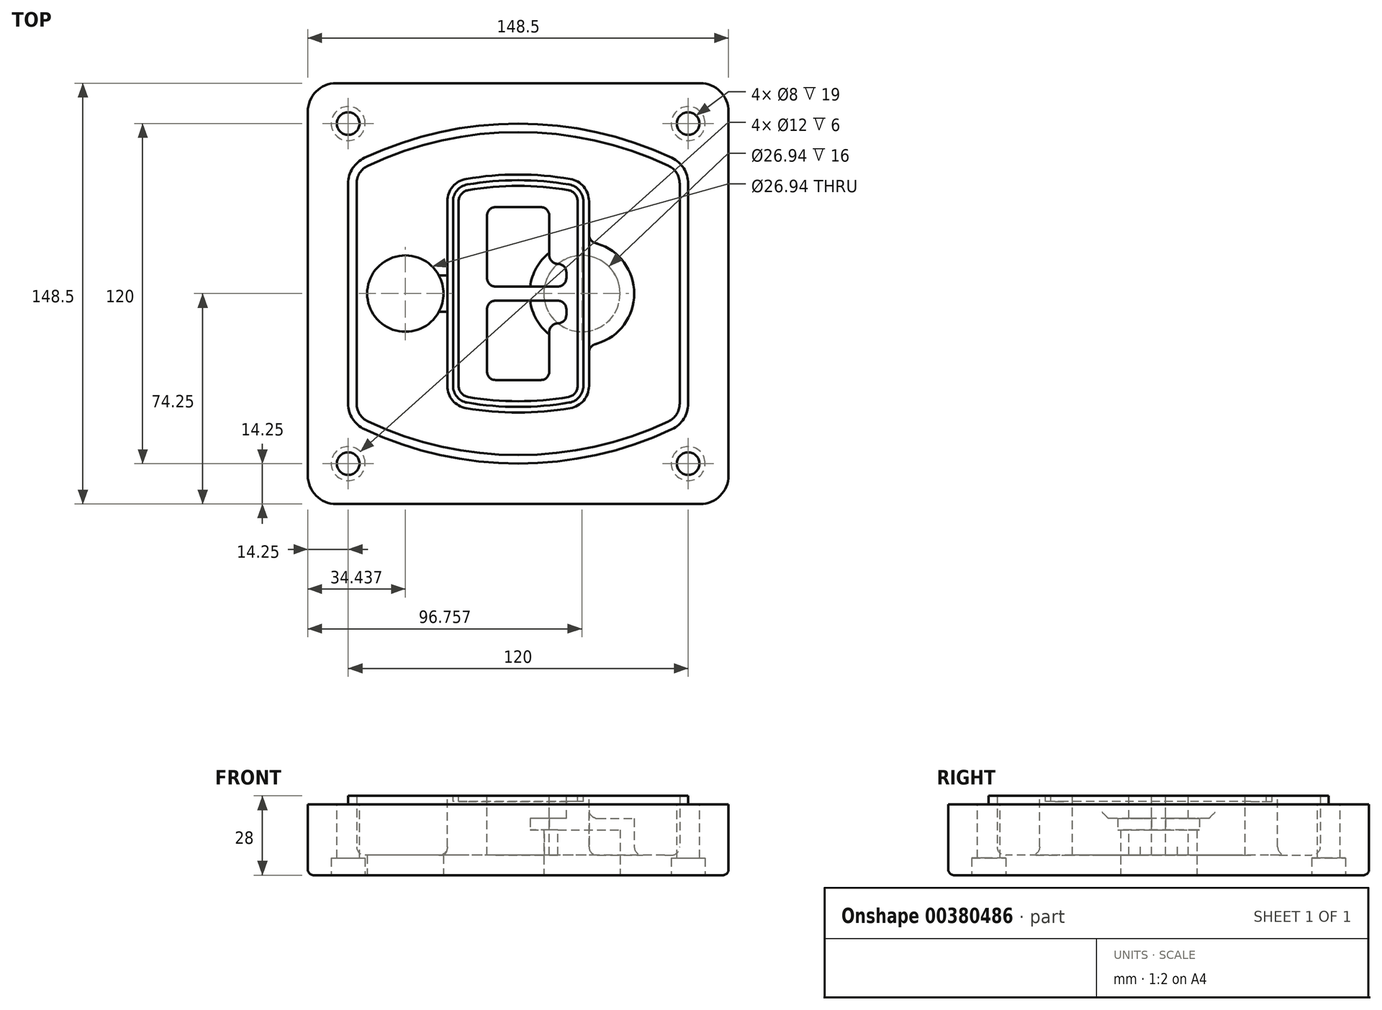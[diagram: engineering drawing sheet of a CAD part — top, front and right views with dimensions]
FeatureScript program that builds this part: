
annotation { "Feature Type Name" : "Feature", "Feature Type Description" : "" }
export const myFeature = defineFeature(function(context is Context, id is Id, definition is map)
    precondition{}
    {
        {
            var Q0;
            Q0=qCreatedBy(makeId("Top.planeOp"),FACE);
            var sketch = newSketch(context, id + "F0", { "sketchPlane" : qUnion([Q0])});
            skPoint(sketch, "E0.rect.middle", {"position": v(0, 0) * mm});
            skLineSegment(sketch, "E1.bottom", {"start": v(-64.25, -74.25) * mm, "end": v(64.25, -74.25) * mm});
            skLineSegment(sketch, "E1.top", {"start": v(-64.25, 74.25) * mm, "end": v(64.25, 74.25) * mm});
            skLineSegment(sketch, "E1.left", {"start": v(-74.25, -64.25) * mm, "end": v(-74.25, 64.25) * mm});
            skLineSegment(sketch, "E1.right", {"start": v(74.25, -64.25) * mm, "end": v(74.25, 64.25) * mm});
            skLineSegment(sketch, "E2", {"start": v(-74.25, 74.25) * mm, "end": v(74.25, -74.25) * mm, "construction": true});
            skLineSegment(sketch, "E3", {"start": v(74.25, 74.25) * mm, "end": v(-74.25, -74.25) * mm, "construction": true});
            skCircle(sketch, "E4", {"center": v(-60, 60) * mm, "radius": 4 * mm});
            skCircle(sketch, "E5", {"center": v(60, 60) * mm, "radius": 4 * mm});
            skCircle(sketch, "E6", {"center": v(60, -60) * mm, "radius": 4 * mm});
            skCircle(sketch, "E7", {"center": v(-60, -60) * mm, "radius": 4 * mm});
            skLineSegment(sketch, "E8", {"start": v(-60, 60) * mm, "end": v(60, 60) * mm, "construction": true});
            skLineSegment(sketch, "E9", {"start": v(60, 60) * mm, "end": v(60, -60) * mm, "construction": true});
            skLineSegment(sketch, "E10", {"start": v(60, -60) * mm, "end": v(-60, -60) * mm, "construction": true});
            skLineSegment(sketch, "E11", {"start": v(-60, -60) * mm, "end": v(-60, 60) * mm, "construction": true});
            skLineSegment(sketch, "E12", {"start": v(-60, 38.83) * mm, "end": v(-60, -38.83) * mm});
            skLineSegment(sketch, "E13", {"start": v(60, 38.83) * mm, "end": v(60, -38.83) * mm});
            skArc(sketch, "E14", {"start": v(54.26, 47.88) * mm, "mid": v(0, 60) * mm, "end": v(-54.26, 47.88) * mm});
            skArc(sketch, "E15", {"start": v(-54.26, -47.88) * mm, "mid": v(0, -60) * mm, "end": v(54.26, -47.88) * mm});
            skLineSegment(sketch, "E16", {"start": v(-60, 0) * mm, "end": v(60, 0) * mm, "construction": true});
            skPoint(sketch, "E17.visualSharp", {"position": v(-60, -45) * mm});
            skArc(sketch, "E17.filletArc", {"start": v(-60, -38.83) * mm, "mid": v(-58.44, -44.2) * mm, "end": v(-54.26, -47.88) * mm});
            skPoint(sketch, "E18.visualSharp", {"position": v(-60, 45) * mm});
            skArc(sketch, "E18.filletArc", {"start": v(-54.26, 47.88) * mm, "mid": v(-58.44, 44.2) * mm, "end": v(-60, 38.83) * mm});
            skPoint(sketch, "E19.visualSharp", {"position": v(60, 45) * mm});
            skArc(sketch, "E19.filletArc", {"start": v(60, 38.83) * mm, "mid": v(58.44, 44.2) * mm, "end": v(54.26, 47.88) * mm});
            skPoint(sketch, "E20.visualSharp", {"position": v(60, -45) * mm});
            skArc(sketch, "E20.filletArc", {"start": v(54.26, -47.88) * mm, "mid": v(58.44, -44.2) * mm, "end": v(60, -38.83) * mm});
            skPoint(sketch, "E21.visualSharp", {"position": v(-74.25, 74.25) * mm});
            skArc(sketch, "E21.filletArc", {"start": v(-64.25, 74.25) * mm, "mid": v(-71.32, 71.32) * mm, "end": v(-74.25, 64.25) * mm});
            skPoint(sketch, "E22.visualSharp", {"position": v(74.25, 74.25) * mm});
            skArc(sketch, "E22.filletArc", {"start": v(74.25, 64.25) * mm, "mid": v(71.32, 71.32) * mm, "end": v(64.25, 74.25) * mm});
            skPoint(sketch, "E23.visualSharp", {"position": v(74.25, -74.25) * mm});
            skArc(sketch, "E23.filletArc", {"start": v(64.25, -74.25) * mm, "mid": v(71.32, -71.32) * mm, "end": v(74.25, -64.25) * mm});
            skPoint(sketch, "E24.visualSharp", {"position": v(-74.25, -74.25) * mm});
            skArc(sketch, "E24.filletArc", {"start": v(-74.25, -64.25) * mm, "mid": v(-71.32, -71.32) * mm, "end": v(-64.25, -74.25) * mm});
            skArc(sketch, "E25.0", {"start": v(57, 38.83) * mm, "mid": v(55.9, 42.58) * mm, "end": v(52.98, 45.17) * mm});
            skLineSegment(sketch, "E25.1", {"start": v(57, 38.83) * mm, "end": v(57, -38.83) * mm});
            skArc(sketch, "E25.2", {"start": v(52.98, -45.17) * mm, "mid": v(55.9, -42.58) * mm, "end": v(57, -38.83) * mm});
            skArc(sketch, "E25.3", {"start": v(-52.98, -45.17) * mm, "mid": v(0, -57) * mm, "end": v(52.98, -45.17) * mm});
            skArc(sketch, "E25.4", {"start": v(-57, -38.83) * mm, "mid": v(-55.9, -42.58) * mm, "end": v(-52.98, -45.17) * mm});
            skArc(sketch, "E25.5", {"start": v(52.98, 45.17) * mm, "mid": v(0, 57) * mm, "end": v(-52.98, 45.17) * mm});
            skLineSegment(sketch, "E25.6", {"start": v(-57, 38.83) * mm, "end": v(-57, -38.83) * mm});
            skArc(sketch, "E25.7", {"start": v(-52.98, 45.17) * mm, "mid": v(-55.9, 42.58) * mm, "end": v(-57, 38.83) * mm});
            skArc(sketch, "E26.0", {"start": v(-55.96, 51.5) * mm, "mid": v(-61.82, 46.33) * mm, "end": v(-64, 38.83) * mm});
            skArc(sketch, "E26.1", {"start": v(55.96, 51.5) * mm, "mid": v(0, 64) * mm, "end": v(-55.96, 51.5) * mm});
            skArc(sketch, "E26.2", {"start": v(64, 38.83) * mm, "mid": v(61.82, 46.33) * mm, "end": v(55.96, 51.5) * mm});
            skLineSegment(sketch, "E26.3", {"start": v(64, 38.83) * mm, "end": v(64, -38.83) * mm});
            skArc(sketch, "E26.4", {"start": v(55.96, -51.5) * mm, "mid": v(61.82, -46.33) * mm, "end": v(64, -38.83) * mm});
            skLineSegment(sketch, "E26.5", {"start": v(-64, 38.83) * mm, "end": v(-64, -38.83) * mm});
            skArc(sketch, "E26.6", {"start": v(-55.96, -51.5) * mm, "mid": v(0, -64) * mm, "end": v(55.96, -51.5) * mm});
            skArc(sketch, "E26.7", {"start": v(-64, -38.83) * mm, "mid": v(-61.82, -46.33) * mm, "end": v(-55.96, -51.5) * mm});
            skLineSegment(sketch, "E27", {"start": v(0, 74.25) * mm, "end": v(0, 104.25) * mm});
            skPoint(sketch, "E27.endSnap0", {"position": v(0, 74.25) * mm});
            skCircle(sketch, "E28", {"center": v(0, 104.25) * mm, "radius": 6 * mm});
            skLineSegment(sketch, "E29", {"start": v(-7.18, 74.25) * mm, "end": v(-7.18, 92.25) * mm});
            skLineSegment(sketch, "E30", {"start": v(-12.94, 92.25) * mm, "end": v(-28.79, 74.25) * mm});
            skLineSegment(sketch, "E31", {"start": v(-12.94, 104.25) * mm, "end": v(-12.94, 92.25) * mm});
            skLineSegment(sketch, "E32", {"start": v(15.13, 92.25) * mm, "end": v(27.03, 74.25) * mm});
            skLineSegment(sketch, "E33", {"start": v(15.13, 92.25) * mm, "end": v(15.13, 104.25) * mm});
            skArc(sketch, "E34", {"start": v(15.13, 104.25) * mm, "mid": v(1.1, 124.55) * mm, "end": v(-12.94, 104.25) * mm});
            skSolve(sketch);
        }
        {
            var Q0;
            Q0=makeQuery(id+"F0.imprint","IMPRINT",FACE,{"disambiguationData":[TD([[makeQuery(id+"F0.imprint","IMPRINT",EDGE,{"derivedFrom":sQuery(id+"F0.wireOp",EDGE,"E1.bottom")}),1.0]])]});
            var Q1;
            Q1=makeQuery(id+"F0.imprint","IMPRINT",FACE,{"disambiguationData":[TD([[makeQuery(id+"F0.imprint","IMPRINT",EDGE,{"derivedFrom":sQuery(id+"F0.wireOp",EDGE,"E12")}),1.0]])]});
            var Q2;
            Q2=makeQuery(id+"F0.imprint","IMPRINT",FACE,{"disambiguationData":[TD([[makeQuery(id+"F0.imprint","IMPRINT",EDGE,{"derivedFrom":sQuery(id+"F0.wireOp",EDGE,"E25.0")}),1.0]])]});
            var Q3;
            Q3=makeQuery(id+"F0.imprint","IMPRINT",FACE,{"disambiguationData":[TD([[makeQuery(id+"F0.imprint","IMPRINT",EDGE,{"derivedFrom":sQuery(id+"F0.wireOp",EDGE,"E12")}),-1.0]])]});
            extrude(context, id + "F1", {"entities" : qUnion([Q0, Q1, Q2, Q3]), "oppositeDirection" : true, "depth" : 25 * mm});
        }
        {
            var Q0;
            Q0=makeQuery(id+"F0.imprint","IMPRINT",FACE,{"disambiguationData":[TD([[makeQuery(id+"F0.imprint","IMPRINT",EDGE,{"derivedFrom":sQuery(id+"F0.wireOp",EDGE,"E12")}),1.0]])]});
            extrude(context, id + "F2", {"entities" : qUnion([Q0]), "operationType" : NewBodyOperationType.ADD, "depth" : 3 * mm});
        }
        {
            var Q0;
            Q0=makeQuery(id+"F0.imprint","IMPRINT",FACE,{"disambiguationData":[TD([[makeQuery(id+"F0.imprint","IMPRINT",EDGE,{"derivedFrom":sQuery(id+"F0.wireOp",EDGE,"E25.0")}),1.0]])]});
            extrude(context, id + "F3", {"entities" : qUnion([Q0]), "operationType" : NewBodyOperationType.REMOVE, "oppositeDirection" : true, "depth" : 18 * mm});
        }
        {
            var Q0;
            Q0=makeQuery(id+"F2.opExtrude","CAP_FACE",FACE,{"disambiguationData":[OSD([sQuery(id+"F0.wireOp",EDGE,"E12"),sQuery(id+"F0.wireOp",EDGE,"E13"),sQuery(id+"F0.wireOp",EDGE,"E14"),sQuery(id+"F0.wireOp",EDGE,"E15"),sQuery(id+"F0.wireOp",EDGE,"E17.filletArc"),sQuery(id+"F0.wireOp",EDGE,"E18.filletArc"),sQuery(id+"F0.wireOp",EDGE,"E19.filletArc"),sQuery(id+"F0.wireOp",EDGE,"E20.filletArc"),sQuery(id+"F0.wireOp",EDGE,"E25.0"),sQuery(id+"F0.wireOp",EDGE,"E25.1"),sQuery(id+"F0.wireOp",EDGE,"E25.2"),sQuery(id+"F0.wireOp",EDGE,"E25.3"),sQuery(id+"F0.wireOp",EDGE,"E25.4"),sQuery(id+"F0.wireOp",EDGE,"E25.5"),sQuery(id+"F0.wireOp",EDGE,"E25.6"),sQuery(id+"F0.wireOp",EDGE,"E25.7")])],"isStart":false});
            var sketch = newSketch(context, id + "F4", { "sketchPlane" : qUnion([Q0])});
            skArc(sketch, "E35.0", {"start": v(-18.34, -40.45) * mm, "mid": v(0, -42) * mm, "end": v(18.34, -40.45) * mm});
            skArc(sketch, "E36.0", {"start": v(18.34, 40.45) * mm, "mid": v(0, 42) * mm, "end": v(-18.34, 40.45) * mm});
            skLineSegment(sketch, "E37", {"start": v(-25, 32.57) * mm, "end": v(-25, -32.57) * mm});
            skLineSegment(sketch, "E38", {"start": v(25, 32.57) * mm, "end": v(25, -32.57) * mm});
            skLineSegment(sketch, "E39", {"start": v(-25, 39.1) * mm, "end": v(25, 39.1) * mm, "construction": true});
            skLineSegment(sketch, "E40", {"start": v(-25, -39.1) * mm, "end": v(25, -39.1) * mm, "construction": true});
            skPoint(sketch, "E41.visualSharp", {"position": v(-25, 39.1) * mm});
            skArc(sketch, "E41.filletArc", {"start": v(-18.34, 40.45) * mm, "mid": v(-23.11, 37.73) * mm, "end": v(-25, 32.57) * mm});
            skPoint(sketch, "E42.visualSharp", {"position": v(25, 39.1) * mm});
            skArc(sketch, "E42.filletArc", {"start": v(25, 32.57) * mm, "mid": v(23.11, 37.73) * mm, "end": v(18.34, 40.45) * mm});
            skPoint(sketch, "E43.visualSharp", {"position": v(25, -39.1) * mm});
            skArc(sketch, "E43.filletArc", {"start": v(18.34, -40.45) * mm, "mid": v(23.11, -37.73) * mm, "end": v(25, -32.57) * mm});
            skPoint(sketch, "E44.visualSharp", {"position": v(-25, -39.1) * mm});
            skArc(sketch, "E44.filletArc", {"start": v(-25, -32.57) * mm, "mid": v(-23.11, -37.73) * mm, "end": v(-18.34, -40.45) * mm});
            skArc(sketch, "E45.0", {"start": v(52.98, 45.17) * mm, "mid": v(0, 57) * mm, "end": v(-52.98, 45.17) * mm});
            skArc(sketch, "E45.1", {"start": v(-52.98, 45.17) * mm, "mid": v(-55.9, 42.58) * mm, "end": v(-57, 38.83) * mm});
            skLineSegment(sketch, "E45.2", {"start": v(-57, 38.83) * mm, "end": v(-57, -38.83) * mm});
            skArc(sketch, "E45.3", {"start": v(-57, -38.83) * mm, "mid": v(-55.9, -42.58) * mm, "end": v(-52.98, -45.17) * mm});
            skArc(sketch, "E45.4", {"start": v(-52.98, -45.17) * mm, "mid": v(0, -57) * mm, "end": v(52.98, -45.17) * mm});
            skArc(sketch, "E45.5", {"start": v(52.98, -45.17) * mm, "mid": v(55.9, -42.58) * mm, "end": v(57, -38.83) * mm});
            skLineSegment(sketch, "E45.6", {"start": v(57, 38.83) * mm, "end": v(57, -38.83) * mm});
            skArc(sketch, "E45.7", {"start": v(57, 38.83) * mm, "mid": v(55.9, 42.58) * mm, "end": v(52.98, 45.17) * mm});
            skLineSegment(sketch, "E46.0", {"start": v(23, 32.57) * mm, "end": v(23, -32.57) * mm});
            skArc(sketch, "E46.1", {"start": v(18, -38.48) * mm, "mid": v(21.58, -36.44) * mm, "end": v(23, -32.57) * mm});
            skArc(sketch, "E46.2", {"start": v(-18, -38.48) * mm, "mid": v(0, -40) * mm, "end": v(18, -38.48) * mm});
            skArc(sketch, "E46.3", {"start": v(-23, -32.57) * mm, "mid": v(-21.58, -36.44) * mm, "end": v(-18, -38.48) * mm});
            skLineSegment(sketch, "E46.4", {"start": v(-23, 32.57) * mm, "end": v(-23, -32.57) * mm});
            skArc(sketch, "E46.5", {"start": v(23, 32.57) * mm, "mid": v(21.58, 36.44) * mm, "end": v(18, 38.48) * mm});
            skArc(sketch, "E46.6", {"start": v(-18, 38.48) * mm, "mid": v(-21.58, 36.44) * mm, "end": v(-23, 32.57) * mm});
            skArc(sketch, "E46.7", {"start": v(18, 38.48) * mm, "mid": v(0, 40) * mm, "end": v(-18, 38.48) * mm});
            skArc(sketch, "E47.0", {"start": v(21, 32.57) * mm, "mid": v(20.06, 35.15) * mm, "end": v(17.67, 36.5) * mm});
            skLineSegment(sketch, "E47.1", {"start": v(21, 32.57) * mm, "end": v(21, -32.57) * mm});
            skArc(sketch, "E47.2", {"start": v(17.67, -36.5) * mm, "mid": v(20.06, -35.15) * mm, "end": v(21, -32.57) * mm});
            skArc(sketch, "E47.3", {"start": v(-17.67, -36.5) * mm, "mid": v(0, -38) * mm, "end": v(17.67, -36.5) * mm});
            skArc(sketch, "E47.4", {"start": v(-21, -32.57) * mm, "mid": v(-20.06, -35.15) * mm, "end": v(-17.67, -36.5) * mm});
            skArc(sketch, "E47.5", {"start": v(17.67, 36.5) * mm, "mid": v(0, 38) * mm, "end": v(-17.67, 36.5) * mm});
            skLineSegment(sketch, "E47.6", {"start": v(-21, 32.57) * mm, "end": v(-21, -32.57) * mm});
            skArc(sketch, "E47.7", {"start": v(-17.67, 36.5) * mm, "mid": v(-20.06, 35.15) * mm, "end": v(-21, 32.57) * mm});
            skLineSegment(sketch, "E48", {"start": v(-25, 0) * mm, "end": v(25, 0) * mm, "construction": true});
            skLineSegment(sketch, "E49", {"start": v(-11, 5.5) * mm, "end": v(-11, 27.5) * mm});
            skLineSegment(sketch, "E50", {"start": v(-8, 30.5) * mm, "end": v(8, 30.5) * mm});
            skLineSegment(sketch, "E51", {"start": v(11, 27.5) * mm, "end": v(11, 13.5) * mm});
            skLineSegment(sketch, "E52", {"start": v(14, 10.5) * mm, "end": v(14, 10.5) * mm});
            skLineSegment(sketch, "E53", {"start": v(17, 7.5) * mm, "end": v(17, 5.5) * mm});
            skLineSegment(sketch, "E54", {"start": v(14, 2.5) * mm, "end": v(-8, 2.5) * mm});
            skPoint(sketch, "E55.visualSharp", {"position": v(-11, 30.5) * mm});
            skArc(sketch, "E55.filletArc", {"start": v(-8, 30.5) * mm, "mid": v(-10.12, 29.62) * mm, "end": v(-11, 27.5) * mm});
            skPoint(sketch, "E56.visualSharp", {"position": v(11, 30.5) * mm});
            skArc(sketch, "E56.filletArc", {"start": v(11, 27.5) * mm, "mid": v(10.12, 29.62) * mm, "end": v(8, 30.5) * mm});
            skPoint(sketch, "E57.visualSharp", {"position": v(11, 10.5) * mm});
            skArc(sketch, "E57.filletArc", {"start": v(11, 13.5) * mm, "mid": v(11.88, 11.38) * mm, "end": v(14, 10.5) * mm});
            skPoint(sketch, "E58.visualSharp", {"position": v(17, 10.5) * mm});
            skArc(sketch, "E58.filletArc", {"start": v(17, 7.5) * mm, "mid": v(16.12, 9.62) * mm, "end": v(14, 10.5) * mm});
            skPoint(sketch, "E59.visualSharp", {"position": v(17, 2.5) * mm});
            skArc(sketch, "E59.filletArc", {"start": v(14, 2.5) * mm, "mid": v(16.12, 3.38) * mm, "end": v(17, 5.5) * mm});
            skPoint(sketch, "E60.visualSharp", {"position": v(-11, 2.5) * mm});
            skArc(sketch, "E60.filletArc", {"start": v(-11, 5.5) * mm, "mid": v(-10.12, 3.38) * mm, "end": v(-8, 2.5) * mm});
            skLineSegment(sketch, "E61.0.MirrorCS", {"start": v(14, -2.5) * mm, "end": v(-8, -2.5) * mm});
            skArc(sketch, "E62.0.MirrorCS", {"start": v(-11, -5.5) * mm, "mid": v(-10.12, -3.38) * mm, "end": v(-8, -2.5) * mm});
            skLineSegment(sketch, "E63.0.MirrorCS", {"start": v(-11, -5.5) * mm, "end": v(-11, -27.5) * mm});
            skArc(sketch, "E64.0.MirrorCS", {"start": v(-8, -30.5) * mm, "mid": v(-10.12, -29.62) * mm, "end": v(-11, -27.5) * mm});
            skLineSegment(sketch, "E65.0.MirrorCS", {"start": v(-8, -30.5) * mm, "end": v(8, -30.5) * mm});
            skArc(sketch, "E66.0.MirrorCS", {"start": v(11, -27.5) * mm, "mid": v(10.12, -29.62) * mm, "end": v(8, -30.5) * mm});
            skLineSegment(sketch, "E67.0.MirrorCS", {"start": v(11, -27.5) * mm, "end": v(11, -13.5) * mm});
            skArc(sketch, "E68.0.MirrorCS", {"start": v(11, -13.5) * mm, "mid": v(11.88, -11.38) * mm, "end": v(14, -10.5) * mm});
            skArc(sketch, "E69.0.MirrorCS", {"start": v(17, -7.5) * mm, "mid": v(16.12, -9.62) * mm, "end": v(14, -10.5) * mm});
            skLineSegment(sketch, "E70.0.MirrorCS", {"start": v(17, -7.5) * mm, "end": v(17, -5.5) * mm});
            skArc(sketch, "E71.0.MirrorCS", {"start": v(14, -2.5) * mm, "mid": v(16.12, -3.38) * mm, "end": v(17, -5.5) * mm});
            skSolve(sketch);
        }
        {
            var Q0;
            Q0=makeQuery(id+"F4.imprint","IMPRINT",FACE,{"disambiguationData":[TD([[makeQuery(id+"F4.imprint","IMPRINT",EDGE,{"derivedFrom":sQuery(id+"F4.wireOp",EDGE,"E35.0")}),1.0]])]});
            var Q1;
            Q1=makeQuery(id+"F4.imprint","IMPRINT",FACE,{"disambiguationData":[TD([[makeQuery(id+"F4.imprint","IMPRINT",EDGE,{"derivedFrom":sQuery(id+"F4.wireOp",EDGE,"E46.0")}),-1.0]])]});
            var Q2;
            Q2=makeQuery(id+"F4.imprint","IMPRINT",FACE,{"disambiguationData":[TD([[makeQuery(id+"F4.imprint","IMPRINT",EDGE,{"derivedFrom":sQuery(id+"F4.wireOp",EDGE,"E47.0")}),1.0]])]});
            extrude(context, id + "F5", {"entities" : qUnion([Q0, Q1, Q2]), "operationType" : NewBodyOperationType.ADD, "endBound" : BoundingType.UP_TO_NEXT, "oppositeDirection" : true, "depth" : 25 * mm});
        }
        {
            var Q0;
            Q0=makeQuery(id+"F4.imprint","IMPRINT",FACE,{"disambiguationData":[TD([[makeQuery(id+"F4.imprint","IMPRINT",EDGE,{"derivedFrom":sQuery(id+"F4.wireOp",EDGE,"E46.0")}),-1.0]])]});
            extrude(context, id + "F6", {"entities" : qUnion([Q0]), "operationType" : NewBodyOperationType.REMOVE, "oppositeDirection" : true, "depth" : 2 * mm});
        }
        {
            var Q0;
            Q0=makeQuery(id+"F1.opExtrude","CAP_FACE",FACE,{"disambiguationData":[OSD([sQuery(id+"F0.wireOp",EDGE,"E1.bottom"),sQuery(id+"F0.wireOp",EDGE,"E1.top"),sQuery(id+"F0.wireOp",EDGE,"E1.left"),sQuery(id+"F0.wireOp",EDGE,"E1.right"),sQuery(id+"F0.wireOp",EDGE,"E4"),sQuery(id+"F0.wireOp",EDGE,"E5"),sQuery(id+"F0.wireOp",EDGE,"E6"),sQuery(id+"F0.wireOp",EDGE,"E7"),sQuery(id+"F0.wireOp",EDGE,"E21.filletArc"),sQuery(id+"F0.wireOp",EDGE,"E22.filletArc"),sQuery(id+"F0.wireOp",EDGE,"E23.filletArc"),sQuery(id+"F0.wireOp",EDGE,"E24.filletArc")])],"isStart":false});
            var sketch = newSketch(context, id + "F7", { "sketchPlane" : qUnion([Q0])});
            skCircle(sketch, "E72", {"center": v(22.5, 0) * mm, "radius": 13.47 * mm});
            skCircle(sketch, "E73", {"center": v(-39.81, 0) * mm, "radius": 13.47 * mm});
            skLineSegment(sketch, "E74", {"start": v(74.25, 0) * mm, "end": v(-74.25, 0) * mm});
            skCircle(sketch, "E75", {"center": v(22.5, 0) * mm, "radius": 18.47 * mm});
            skCircle(sketch, "E76", {"center": v(60, -60) * mm, "radius": 6 * mm});
            skCircle(sketch, "E77", {"center": v(-60, -60) * mm, "radius": 6 * mm});
            skCircle(sketch, "E78", {"center": v(-60, 60) * mm, "radius": 6 * mm});
            skCircle(sketch, "E79", {"center": v(60, 60) * mm, "radius": 6 * mm});
            skSolve(sketch);
        }
        {
            var Q0;
            {var subQ1=sQuery(id+"F7.wireOp",EDGE,"E74");var subQ4=sQuery(id+"F7.wireOp",EDGE,"E72");var subQ6=makeQuery(id+"F7.imprint","INTERSECT",VERTEX,{"disambiguationData":[OD(0.0)],"derivedFrom":[subQ4,subQ1]});Q0=makeQuery(id+"F7.imprint","IMPRINT",FACE,{"disambiguationData":[TD([[makeQuery(id+"F7.imprint","IMPRINT",EDGE,{"disambiguationData":[TD([[subQ6,-1.0]])],"derivedFrom":subQ4}),-1.0]])]});}
            var Q1;
            {var subQ0=sQuery(id+"F7.wireOp",EDGE,"E74");var subQ1=sQuery(id+"F7.wireOp",EDGE,"E72");var subQ3=makeQuery(id+"F7.imprint","INTERSECT",VERTEX,{"disambiguationData":[OD(0.0)],"derivedFrom":[subQ1,subQ0]});Q1=makeQuery(id+"F7.imprint","IMPRINT",FACE,{"disambiguationData":[TD([[makeQuery(id+"F7.imprint","IMPRINT",EDGE,{"disambiguationData":[TD([[subQ3,-1.0]])],"derivedFrom":subQ1}),1.0]])]});}
            var Q2;
            {var subQ0=sQuery(id+"F7.wireOp",EDGE,"E74");var subQ1=sQuery(id+"F7.wireOp",EDGE,"E72");var subQ3=makeQuery(id+"F7.imprint","INTERSECT",VERTEX,{"disambiguationData":[OD(0.0)],"derivedFrom":[subQ1,subQ0]});Q2=makeQuery(id+"F7.imprint","IMPRINT",FACE,{"disambiguationData":[TD([[makeQuery(id+"F7.imprint","IMPRINT",EDGE,{"disambiguationData":[TD([[subQ3,1.0]])],"derivedFrom":subQ1}),1.0]])]});}
            var Q3;
            {var subQ1=sQuery(id+"F7.wireOp",EDGE,"E74");var subQ4=sQuery(id+"F7.wireOp",EDGE,"E72");var subQ6=makeQuery(id+"F7.imprint","INTERSECT",VERTEX,{"disambiguationData":[OD(0.0)],"derivedFrom":[subQ4,subQ1]});Q3=makeQuery(id+"F7.imprint","IMPRINT",FACE,{"disambiguationData":[TD([[makeQuery(id+"F7.imprint","IMPRINT",EDGE,{"disambiguationData":[TD([[subQ6,1.0]])],"derivedFrom":subQ4}),-1.0]])]});}
            extrude(context, id + "F8", {"entities" : qUnion([Q0, Q1, Q2, Q3]), "operationType" : NewBodyOperationType.ADD, "oppositeDirection" : true, "depth" : 20 * mm});
        }
        {
            var Q0;
            {var subQ0=sQuery(id+"F7.wireOp",EDGE,"E74");var subQ1=sQuery(id+"F7.wireOp",EDGE,"E72");var subQ3=makeQuery(id+"F7.imprint","INTERSECT",VERTEX,{"disambiguationData":[OD(0.0)],"derivedFrom":[subQ1,subQ0]});Q0=makeQuery(id+"F7.imprint","IMPRINT",FACE,{"disambiguationData":[TD([[makeQuery(id+"F7.imprint","IMPRINT",EDGE,{"disambiguationData":[TD([[subQ3,-1.0]])],"derivedFrom":subQ1}),1.0]])]});}
            var Q1;
            {var subQ0=sQuery(id+"F7.wireOp",EDGE,"E74");var subQ1=sQuery(id+"F7.wireOp",EDGE,"E72");var subQ3=makeQuery(id+"F7.imprint","INTERSECT",VERTEX,{"disambiguationData":[OD(0.0)],"derivedFrom":[subQ1,subQ0]});Q1=makeQuery(id+"F7.imprint","IMPRINT",FACE,{"disambiguationData":[TD([[makeQuery(id+"F7.imprint","IMPRINT",EDGE,{"disambiguationData":[TD([[subQ3,1.0]])],"derivedFrom":subQ1}),1.0]])]});}
            extrude(context, id + "F9", {"entities" : qUnion([Q0, Q1]), "operationType" : NewBodyOperationType.REMOVE, "oppositeDirection" : true, "depth" : 16 * mm});
        }
        {
            var Q0;
            {var subQ0=sQuery(id+"F7.wireOp",EDGE,"E74");var subQ1=sQuery(id+"F7.wireOp",EDGE,"E73");var subQ3=makeQuery(id+"F7.imprint","INTERSECT",VERTEX,{"disambiguationData":[OD(0.0)],"derivedFrom":[subQ1,subQ0]});Q0=makeQuery(id+"F7.imprint","IMPRINT",FACE,{"disambiguationData":[TD([[makeQuery(id+"F7.imprint","IMPRINT",EDGE,{"disambiguationData":[TD([[subQ3,-1.0]])],"derivedFrom":subQ1}),1.0]])]});}
            var Q1;
            {var subQ0=sQuery(id+"F7.wireOp",EDGE,"E74");var subQ1=sQuery(id+"F7.wireOp",EDGE,"E73");var subQ3=makeQuery(id+"F7.imprint","INTERSECT",VERTEX,{"disambiguationData":[OD(0.0)],"derivedFrom":[subQ1,subQ0]});Q1=makeQuery(id+"F7.imprint","IMPRINT",FACE,{"disambiguationData":[TD([[makeQuery(id+"F7.imprint","IMPRINT",EDGE,{"disambiguationData":[TD([[subQ3,1.0]])],"derivedFrom":subQ1}),1.0]])]});}
            extrude(context, id + "F10", {"entities" : qUnion([Q0, Q1]), "operationType" : NewBodyOperationType.REMOVE, "oppositeDirection" : true, "depth" : 25 * mm});
        }
        {
            var Q0;
            Q0=makeQuery(id+"F7.imprint","IMPRINT",FACE,{"disambiguationData":[TD([[makeQuery(id+"F7.imprint","IMPRINT",EDGE,{"derivedFrom":sQuery(id+"F7.wireOp",EDGE,"E76")}),1.0]])]});
            var Q1;
            Q1=makeQuery(id+"F7.imprint","IMPRINT",FACE,{"disambiguationData":[TD([[makeQuery(id+"F7.imprint","IMPRINT",EDGE,{"derivedFrom":makeQuery(id+"F1.opExtrude","CAP_EDGE",EDGE,{"disambiguationData":[OSD([sQuery(id+"F0.wireOp",EDGE,"E5")])],"isStart":false})}),-1.0]])]});
            var Q2;
            Q2=makeQuery(id+"F7.imprint","IMPRINT",FACE,{"disambiguationData":[TD([[makeQuery(id+"F7.imprint","IMPRINT",EDGE,{"derivedFrom":sQuery(id+"F7.wireOp",EDGE,"E77")}),1.0]])]});
            var Q3;
            Q3=makeQuery(id+"F7.imprint","IMPRINT",FACE,{"disambiguationData":[TD([[makeQuery(id+"F7.imprint","IMPRINT",EDGE,{"derivedFrom":makeQuery(id+"F1.opExtrude","CAP_EDGE",EDGE,{"disambiguationData":[OSD([sQuery(id+"F0.wireOp",EDGE,"E4")])],"isStart":false})}),-1.0]])]});
            var Q4;
            Q4=makeQuery(id+"F7.imprint","IMPRINT",FACE,{"disambiguationData":[TD([[makeQuery(id+"F7.imprint","IMPRINT",EDGE,{"derivedFrom":sQuery(id+"F7.wireOp",EDGE,"E78")}),1.0]])]});
            var Q5;
            Q5=makeQuery(id+"F7.imprint","IMPRINT",FACE,{"disambiguationData":[TD([[makeQuery(id+"F7.imprint","IMPRINT",EDGE,{"derivedFrom":makeQuery(id+"F1.opExtrude","CAP_EDGE",EDGE,{"disambiguationData":[OSD([sQuery(id+"F0.wireOp",EDGE,"E7")])],"isStart":false})}),-1.0]])]});
            var Q6;
            Q6=makeQuery(id+"F7.imprint","IMPRINT",FACE,{"disambiguationData":[TD([[makeQuery(id+"F7.imprint","IMPRINT",EDGE,{"derivedFrom":sQuery(id+"F7.wireOp",EDGE,"E79")}),1.0]])]});
            var Q7;
            Q7=makeQuery(id+"F7.imprint","IMPRINT",FACE,{"disambiguationData":[TD([[makeQuery(id+"F7.imprint","IMPRINT",EDGE,{"derivedFrom":makeQuery(id+"F1.opExtrude","CAP_EDGE",EDGE,{"disambiguationData":[OSD([sQuery(id+"F0.wireOp",EDGE,"E6")])],"isStart":false})}),-1.0]])]});
            extrude(context, id + "F11", {"entities" : qUnion([Q0, Q1, Q2, Q3, Q4, Q5, Q6, Q7]), "operationType" : NewBodyOperationType.REMOVE, "oppositeDirection" : true, "depth" : 6 * mm});
        }
        {
            var Q0;
            Q0=makeQuery(id+"F9.boolean.opBoolean","COPY",FACE,{"derivedFrom":makeQuery(id+"F9.opExtrude","CAP_FACE",FACE,{"disambiguationData":[OSD([sQuery(id+"F7.wireOp",EDGE,"E72")])],"isStart":false})});
            var sketch = newSketch(context, id + "F12", { "sketchPlane" : qUnion([Q0])});
            skArc(sketch, "E80.0", {"start": v(11, 14.45) * mm, "mid": v(6.45, 9.13) * mm, "end": v(4.2, 2.5) * mm});
            skArc(sketch, "E80.1", {"start": v(4.2, -2.5) * mm, "mid": v(6.45, -9.13) * mm, "end": v(11, -14.45) * mm});
            skLineSegment(sketch, "E81", {"start": v(4.2, -2.5) * mm, "end": v(14, -2.5) * mm});
            skLineSegment(sketch, "E82.0", {"start": v(14, 2.5) * mm, "end": v(4.2, 2.5) * mm});
            skArc(sketch, "E82.1", {"start": v(14, 2.5) * mm, "mid": v(16.12, 3.38) * mm, "end": v(17, 5.5) * mm});
            skLineSegment(sketch, "E82.2", {"start": v(17, 7.5) * mm, "end": v(17, 5.5) * mm});
            skArc(sketch, "E82.3", {"start": v(17, 7.5) * mm, "mid": v(16.12, 9.62) * mm, "end": v(14, 10.5) * mm});
            skArc(sketch, "E82.4", {"start": v(11, 13.5) * mm, "mid": v(11.88, 11.38) * mm, "end": v(14, 10.5) * mm});
            skLineSegment(sketch, "E82.5", {"start": v(11, 14.45) * mm, "end": v(11, 13.5) * mm});
            skLineSegment(sketch, "E82.7", {"start": v(14, -2.5) * mm, "end": v(4.2, -2.5) * mm});
            skArc(sketch, "E82.8", {"start": v(14, -2.5) * mm, "mid": v(16.12, -3.38) * mm, "end": v(17, -5.5) * mm});
            skLineSegment(sketch, "E82.9", {"start": v(17, -7.5) * mm, "end": v(17, -5.5) * mm});
            skArc(sketch, "E82.10", {"start": v(17, -7.5) * mm, "mid": v(16.12, -9.62) * mm, "end": v(14, -10.5) * mm});
            skArc(sketch, "E82.11", {"start": v(11, -13.5) * mm, "mid": v(11.88, -11.38) * mm, "end": v(14, -10.5) * mm});
            skLineSegment(sketch, "E82.12", {"start": v(11, -14.45) * mm, "end": v(11, -13.5) * mm});
            skPoint(sketch, "E83.orphan", {"position": v(11, -27.5) * mm});
            skPoint(sketch, "E84.orphan", {"position": v(-8, -2.5) * mm});
            skPoint(sketch, "E85.orphan", {"position": v(-8, 2.5) * mm});
            skPoint(sketch, "E86.orphan", {"position": v(11, 27.5) * mm});
            skSolve(sketch);
        }
        {
            var Q0;
            {var subQ7=sQuery(id+"F12.wireOp",EDGE,"E80.0");var subQ14=sQuery(id+"F12.wireOp",EDGE,"E80.1");var subQ16=sQuery(id+"F12.wireOp",EDGE,"E82.1");var subQ18=sQuery(id+"F12.wireOp",EDGE,"E82.8");Q0=qUnion([makeQuery(id+"F12.imprint","IMPRINT",FACE,{"disambiguationData":[TD([[makeQuery(id+"F12.imprint","IMPRINT",EDGE,{"derivedFrom":subQ7}),1.0]])]}),makeQuery(id+"F12.imprint","IMPRINT",FACE,{"disambiguationData":[TD([[makeQuery(id+"F12.imprint","IMPRINT",EDGE,{"derivedFrom":subQ14}),1.0]])]}),makeQuery(id+"F12.imprint","IMPRINT",FACE,{"disambiguationData":[TD([[makeQuery(id+"F12.imprint","IMPRINT",EDGE,{"derivedFrom":subQ16}),1.0]])]}),makeQuery(id+"F12.imprint","IMPRINT",FACE,{"disambiguationData":[TD([[makeQuery(id+"F12.imprint","IMPRINT",EDGE,{"derivedFrom":subQ18}),-1.0]])]})]);}
            var Q1;
            Q1=makeQuery(id+"F5.boolean.opBoolean","SPLIT",FACE,{"disambiguationData":[TD([makeQuery(id+"F5.opExtrude","SWEPT_FACE",FACE,{"disambiguationData":[OSD([sQuery(id+"F4.wireOp",EDGE,"E49")])]})])],"derivedFrom":makeQuery(id+"F3.boolean.opBoolean","COPY",FACE,{"derivedFrom":makeQuery(id+"F3.opExtrude","CAP_FACE",FACE,{"disambiguationData":[OSD([sQuery(id+"F0.wireOp",EDGE,"E25.0"),sQuery(id+"F0.wireOp",EDGE,"E25.1"),sQuery(id+"F0.wireOp",EDGE,"E25.2"),sQuery(id+"F0.wireOp",EDGE,"E25.3"),sQuery(id+"F0.wireOp",EDGE,"E25.4"),sQuery(id+"F0.wireOp",EDGE,"E25.5"),sQuery(id+"F0.wireOp",EDGE,"E25.6"),sQuery(id+"F0.wireOp",EDGE,"E25.7")])],"isStart":false})})});
            extrude(context, id + "F13", {"entities" : qUnion([Q0]), "operationType" : NewBodyOperationType.REMOVE, "endBound" : BoundingType.UP_TO_SURFACE, "endBoundEntityFace" : qUnion([Q1]), "depth" : 25 * mm});
        }
        {
            var Q0;
            Q0=makeQuery(id+"F3.boolean.opBoolean","COPY",EDGE,{"derivedFrom":makeQuery(id+"F3.opExtrude","CAP_EDGE",EDGE,{"disambiguationData":[OSD([sQuery(id+"F0.wireOp",EDGE,"E25.6")])],"isStart":false})});
            var Q1;
            Q1=makeQuery(id+"F8.boolean.opBoolean","INTERSECT",EDGE,{"derivedFrom":[makeQuery(id+"F5.opExtrude","SWEPT_FACE",FACE,{"disambiguationData":[OSD([sQuery(id+"F4.wireOp",EDGE,"E38")])]}),makeQuery(id+"F8.opExtrude","CAP_FACE",FACE,{"disambiguationData":[OSD([sQuery(id+"F7.wireOp",EDGE,"E75")])],"isStart":false})]});
            var Q2;
            Q2=makeQuery(id+"F8.boolean.opBoolean","INTERSECT",EDGE,{"disambiguationData":[OD(1.0)],"derivedFrom":[makeQuery(id+"F5.opExtrude","SWEPT_FACE",FACE,{"disambiguationData":[OSD([sQuery(id+"F4.wireOp",EDGE,"E38")])]}),makeQuery(id+"F8.opExtrude","SWEPT_FACE",FACE,{"disambiguationData":[OSD([sQuery(id+"F7.wireOp",EDGE,"E75")])]})]});
            var Q3;
            {var subQ0=sQuery(id+"F4.wireOp",EDGE,"E38");Q3=makeQuery(id+"F8.boolean.opBoolean","SPLIT",EDGE,{"disambiguationData":[TD([makeQuery(id+"F5.opExtrude","SWEPT_FACE",FACE,{"disambiguationData":[OSD([sQuery(id+"F4.wireOp",EDGE,"E43.filletArc")])]})])],"derivedFrom":makeQuery(id+"F5.opExtrude","CAP_EDGE",EDGE,{"disambiguationData":[OSD([subQ0])],"isStart":false})});}
            var Q4;
            {var subQ0=sQuery(id+"F0.wireOp",EDGE,"E25.7");var subQ1=sQuery(id+"F0.wireOp",EDGE,"E25.1");var subQ2=sQuery(id+"F0.wireOp",EDGE,"E25.6");var subQ3=sQuery(id+"F0.wireOp",EDGE,"E25.5");var subQ4=sQuery(id+"F0.wireOp",EDGE,"E25.4");var subQ5=sQuery(id+"F0.wireOp",EDGE,"E25.0");var subQ6=sQuery(id+"F0.wireOp",EDGE,"E25.2");var subQ7=sQuery(id+"F0.wireOp",EDGE,"E25.3");Q4=makeQuery(id+"F8.boolean.opBoolean","INTERSECT",EDGE,{"derivedFrom":[makeQuery(id+"F5.boolean.opBoolean","SPLIT",FACE,{"disambiguationData":[TD([makeQuery(id+"F2.opExtrude","SWEPT_FACE",FACE,{"disambiguationData":[OSD([subQ5])]})])],"derivedFrom":makeQuery(id+"F3.boolean.opBoolean","COPY",FACE,{"derivedFrom":makeQuery(id+"F3.opExtrude","CAP_FACE",FACE,{"disambiguationData":[OSD([subQ5,subQ1,subQ6,subQ7,subQ4,subQ3,subQ2,subQ0])],"isStart":false})})}),makeQuery(id+"F8.opExtrude","SWEPT_FACE",FACE,{"disambiguationData":[OSD([sQuery(id+"F7.wireOp",EDGE,"E75")])]})]});}
            var Q5;
            Q5=makeQuery(id+"F8.boolean.opBoolean","INTERSECT",EDGE,{"disambiguationData":[OD(0.0)],"derivedFrom":[makeQuery(id+"F5.opExtrude","SWEPT_FACE",FACE,{"disambiguationData":[OSD([sQuery(id+"F4.wireOp",EDGE,"E38")])]}),makeQuery(id+"F8.opExtrude","SWEPT_FACE",FACE,{"disambiguationData":[OSD([sQuery(id+"F7.wireOp",EDGE,"E75")])]})]});
            fillet(context, id + "F14", {"entities" : qUnion([Q0, Q1, Q2, Q3, Q4, Q5]), "radius" : 3 * mm, "tangentPropagation" : true, "allowEdgeOverflow" : false});
        }
        {
            var Q0;
            Q0=makeQuery(id+"F1.opExtrude","CAP_EDGE",EDGE,{"disambiguationData":[OSD([sQuery(id+"F0.wireOp",EDGE,"E1.bottom")])],"isStart":false});
            fillet(context, id + "F15", {"entities" : qUnion([Q0]), "radius" : 2 * mm, "tangentPropagation" : true, "allowEdgeOverflow" : false});
        }
    });
